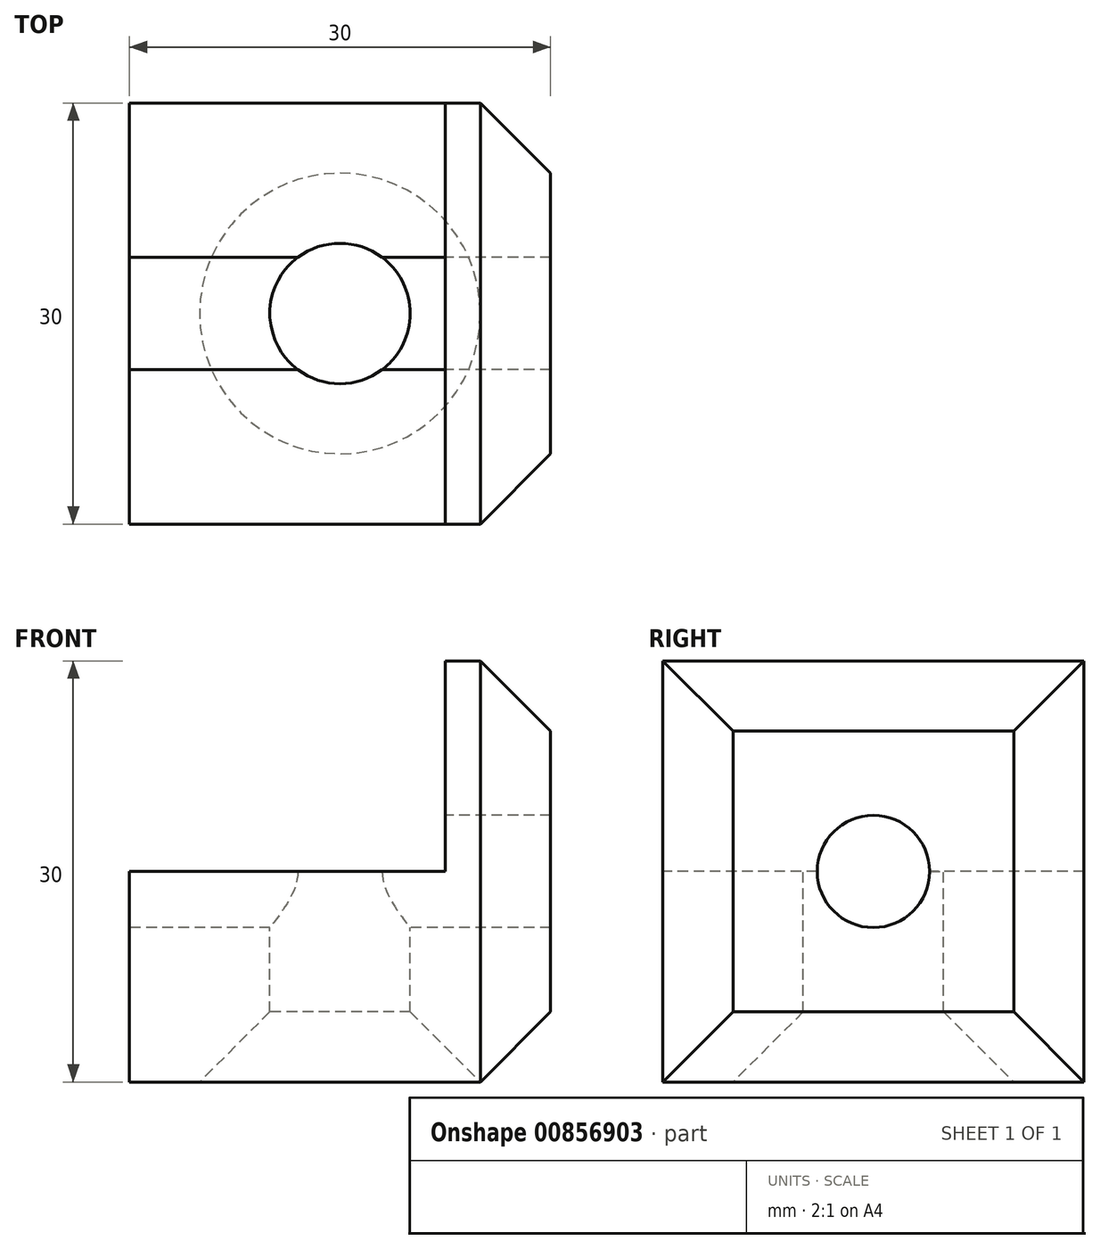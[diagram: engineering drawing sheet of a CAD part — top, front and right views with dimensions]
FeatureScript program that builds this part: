
annotation { "Feature Type Name" : "Feature", "Feature Type Description" : "" }
export const myFeature = defineFeature(function(context is Context, id is Id, definition is map)
    precondition{}
    {
        {
            var Q0;
            Q0=qCreatedBy(makeId("Top.planeOp"),FACE);
            var sketch = newSketch(context, id + "F0", { "sketchPlane" : qUnion([Q0])});
            skLineSegment(sketch, "E0.bottom", {"start": v(-14.57, 7.14) * mm, "end": v(15.43, 7.14) * mm});
            skLineSegment(sketch, "E0.top", {"start": v(-14.57, -22.86) * mm, "end": v(15.43, -22.86) * mm});
            skLineSegment(sketch, "E0.left", {"start": v(-14.57, 7.14) * mm, "end": v(-14.57, -22.86) * mm});
            skLineSegment(sketch, "E0.right", {"start": v(15.43, 7.14) * mm, "end": v(15.43, -22.86) * mm});
            skSolve(sketch);
        }
        {
            var Q0;
            Q0 = qSketchRegion(id + "F0", true);
            extrude(context, id + "F1", {"entities" : qUnion([Q0]), "depth" : 30 * mm, "offsetDistance" : 25 * mm});
        }
        {
            var Q0;
            Q0=makeQuery(id+"F1.opExtrude","SWEPT_FACE",FACE,{"disambiguationData":[OSD([sQuery(id+"F0.wireOp",EDGE,"E0.left")])]});
            var sketch = newSketch(context, id + "F2", { "sketchPlane" : qUnion([Q0])});
            skCircle(sketch, "E1", {"center": v(7.86, 15) * mm, "radius": 4 * mm});
            skPoint(sketch, "E1.centerSnap0", {"position": v(-7.14, 15) * mm});
            skPoint(sketch, "E1.centerSnap1", {"position": v(7.86, 30) * mm});
            skSolve(sketch);
        }
        {
            var Q0;
            Q0 = qSketchRegion(id + "F2", true);
            extrude(context, id + "F3", {"entities" : qUnion([Q0]), "operationType" : NewBodyOperationType.REMOVE, "endBound" : BoundingType.THROUGH_ALL, "oppositeDirection" : true, "depth" : 25 * mm, "offsetDistance" : 25 * mm});
        }
        {
            var Q0;
            Q0=makeQuery(id+"F1.opExtrude","CAP_FACE",FACE,{"disambiguationData":[OSD([sQuery(id+"F0.wireOp",EDGE,"E0.bottom"),sQuery(id+"F0.wireOp",EDGE,"E0.top"),sQuery(id+"F0.wireOp",EDGE,"E0.left"),sQuery(id+"F0.wireOp",EDGE,"E0.right")])],"isStart":false});
            var sketch = newSketch(context, id + "F4", { "sketchPlane" : qUnion([Q0])});
            skCircle(sketch, "E2", {"center": v(0.43, -7.86) * mm, "radius": 5 * mm});
            skPoint(sketch, "E2.centerSnap0", {"position": v(0.43, 7.14) * mm});
            skPoint(sketch, "E2.centerSnap1", {"position": v(-14.57, -7.86) * mm});
            skSolve(sketch);
        }
        {
            var Q0;
            Q0 = qSketchRegion(id + "F4", true);
            extrude(context, id + "F5", {"entities" : qUnion([Q0]), "operationType" : NewBodyOperationType.REMOVE, "endBound" : BoundingType.THROUGH_ALL, "oppositeDirection" : true, "depth" : 25 * mm, "offsetDistance" : 25 * mm});
        }
        {
            var Q0;
            Q0=makeQuery(id+"F1.opExtrude","SWEPT_FACE",FACE,{"disambiguationData":[OSD([sQuery(id+"F0.wireOp",EDGE,"E0.left")])]});
            var sketch = newSketch(context, id + "F6", { "sketchPlane" : qUnion([Q0])});
            skLineSegment(sketch, "E3.bottom", {"start": v(-7.14, 15) * mm, "end": v(22.86, 15) * mm});
            skLineSegment(sketch, "E3.top", {"start": v(-7.14, 30) * mm, "end": v(22.86, 30) * mm});
            skLineSegment(sketch, "E3.left", {"start": v(-7.14, 15) * mm, "end": v(-7.14, 30) * mm});
            skLineSegment(sketch, "E3.right", {"start": v(22.86, 15) * mm, "end": v(22.86, 30) * mm});
            skSolve(sketch);
        }
        {
            var Q0;
            Q0 = qSketchRegion(id + "F6", true);
            extrude(context, id + "F7", {"entities" : qUnion([Q0]), "operationType" : NewBodyOperationType.REMOVE, "oppositeDirection" : true, "depth" : 22.5 * mm, "offsetDistance" : 25 * mm});
        }
        {
            var Q0;
            Q0=makeQuery(id+"F5.boolean.opBoolean","INTERSECT",EDGE,{"derivedFrom":[makeQuery(id+"F1.opExtrude","CAP_FACE",FACE,{"disambiguationData":[OSD([sQuery(id+"F0.wireOp",EDGE,"E0.bottom"),sQuery(id+"F0.wireOp",EDGE,"E0.top"),sQuery(id+"F0.wireOp",EDGE,"E0.left"),sQuery(id+"F0.wireOp",EDGE,"E0.right")])],"isStart":true}),makeQuery(id+"F5.opExtrude","SWEPT_FACE",FACE,{"disambiguationData":[OSD([sQuery(id+"F4.wireOp",EDGE,"E2")])]})]});
            chamfer(context, id + "F8", {"entities" : qUnion([Q0]), "width" : 5 * mm, "tangentPropagation" : true});
        }
        {
            var Q0;
            Q0=makeQuery(id+"F1.opExtrude","CAP_EDGE",EDGE,{"disambiguationData":[OSD([sQuery(id+"F0.wireOp",EDGE,"E0.right")])],"isStart":false});
            var Q1;
            Q1=makeQuery(id+"F1.opExtrude","SWEPT_EDGE",EDGE,{"disambiguationData":[OSD([sQuery(id+"F0.wireOp",EDGE,"E0.top"),sQuery(id+"F0.wireOp",EDGE,"E0.right")])]});
            var Q2;
            Q2=makeQuery(id+"F1.opExtrude","SWEPT_EDGE",EDGE,{"disambiguationData":[OSD([sQuery(id+"F0.wireOp",EDGE,"E0.bottom"),sQuery(id+"F0.wireOp",EDGE,"E0.right")])]});
            var Q3;
            Q3=makeQuery(id+"F1.opExtrude","CAP_EDGE",EDGE,{"disambiguationData":[OSD([sQuery(id+"F0.wireOp",EDGE,"E0.right")])],"isStart":true});
            chamfer(context, id + "F9", {"entities" : qUnion([Q0, Q1, Q2, Q3]), "width" : 5 * mm, "tangentPropagation" : true});
        }
    });
